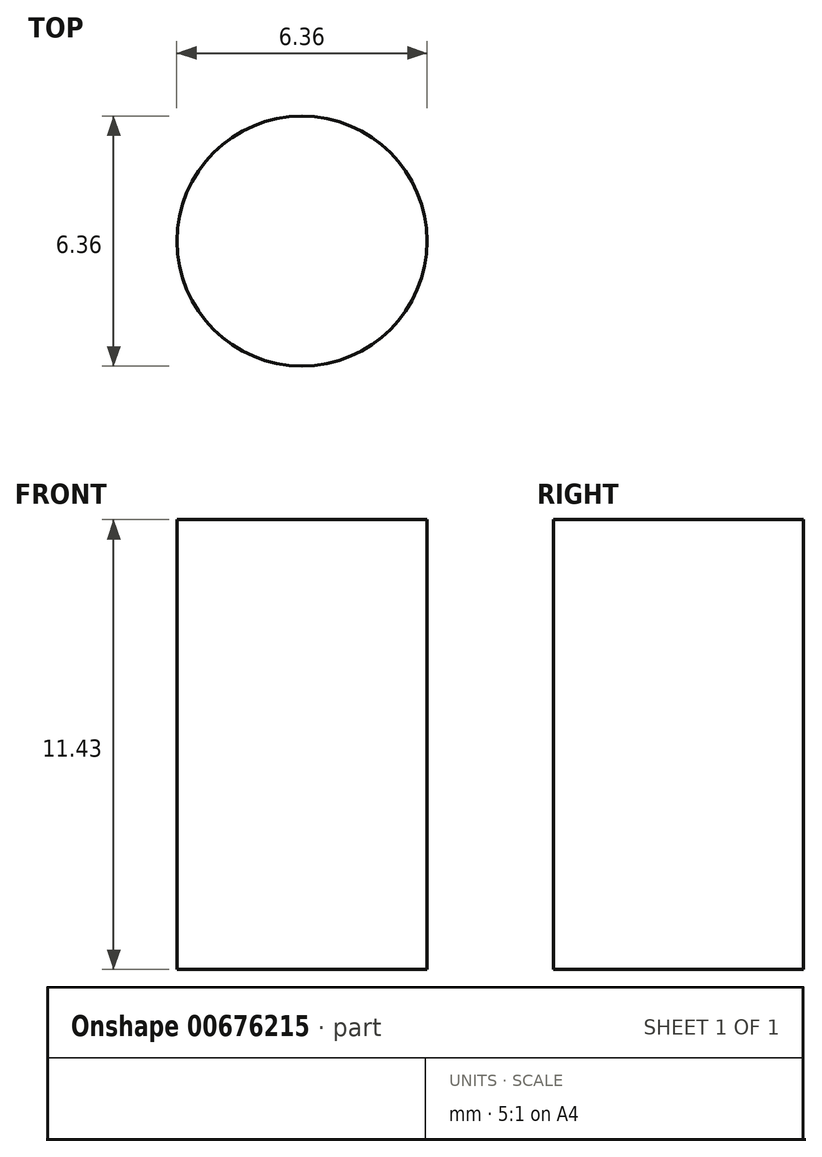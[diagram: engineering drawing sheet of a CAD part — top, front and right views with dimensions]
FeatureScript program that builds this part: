
annotation { "Feature Type Name" : "Feature", "Feature Type Description" : "" }
export const myFeature = defineFeature(function(context is Context, id is Id, definition is map)
    precondition{}
    {
        {
            var Q0;
            Q0=qCreatedBy(makeId("Top.planeOp"),FACE);
            var sketch = newSketch(context, id + "F0", { "sketchPlane" : qUnion([Q0])});
            skCircle(sketch, "E0", {"center": v(0, 0) * mm, "radius": 3.18 * mm});
            skSolve(sketch);
        }
        {
            var Q0;
            Q0=makeQuery(id+"F0.imprint","IMPRINT",FACE,{"disambiguationData":[TD([[makeQuery(id+"F0.imprint","IMPRINT",EDGE,{"derivedFrom":sQuery(id+"F0.wireOp",EDGE,"E0")}),1.0]])]});
            extrude(context, id + "F1", {"entities" : qUnion([Q0]), "depth" : 11.43 * mm, "offsetDistance" : 25.4 * mm});
        }
    });
